# Revit family: Atlas_Sound_AHSUB15-BSG
name_source: partatom
category: Communication Devices
units: mm (PartAtom-declared; Revit-internal decimal feet)

## family parameters
Always vertical = No
Cut with Voids When Loaded = No
Maintain Annotation Orientation = No
Part Type = Normal
Room Calculation Point = No
Round Connector Dimension = Use Diameter
Shared = No
Work Plane-Based = Yes

## types (1)
- Full-Range, Outdoor, Horn Loudspeaker
    100V Taps = 32.00 W
    70V Taps = 32.00 W
    Baffle Material = <By Category>
    Body Material = Default
    Color = <By Category>
    Cost = 2200.99 $
    Cost MSRP = 2200.99 $
    Coverage Horizontal = 0.00°
    Coverage Vertical = 0.00°
    Default Elevation = 48 "
    Depth = 30.56 "
    Description = 15" AH SERIES STADIUM SUBWOOFER SYSTEM
    Dispersion Angle = 0.00°
    Enclosure Material = <By Category>
    Family Code (default) = LOUD SPEAKERS
    Frequency Response  = 55Hz – 120Hz (±5dB)
    Grill Material = QF_Plastic - Black - Fine Textured
    Height = 0.65 "
    IQ Category = SPEAKERS
    Impedance = 8
    Ingress Protection = IP45 When Tilted 5° Downwards
    Input Connectors = Barrier Terminal
    Manufacturer = ATLAS SOUND
    Manufacturer URL = https://www.atlasied.com
    Market = Commercial, Higher Education, Emergency
    MasterFormat = 27 41 13
    MaterFormat Title = SPEAKERS
    Max Input Ratings (8Ω) = TBD
    Maximum Output = 127dB
    Model = AHSUB15-BSG
    Mount Material = Default
    OmniClass Number = 23-37 17 13 19
    OmniClass Title = SPEAKERS
    Pitch = 0.00°
    Power Peak = 500
    Power Rating (RMS) = 250 Watts RMS
    Product Documentation Link = https://www.atlasied.com
    Product Page URL = https://www.atlasied.com
    Rotation = 0.00°
    SPL Max = 107
    ScheduleType |RF| = AtlasIED Master
    Sensitivity = 103
    Speaker Dispersion = 120.00°
    Speaker Type = S1
    Transformer Option = Yes
    URL = www.atlassound.com
    Vertical Symmetry = Yes
    Warranty = 5 Year
    Weight Product = 280
    Width = 30 "

## geometry (parser evidence)
native form markers: Blend x4, Sweep x2
no freeform markers — native parametric forms only
